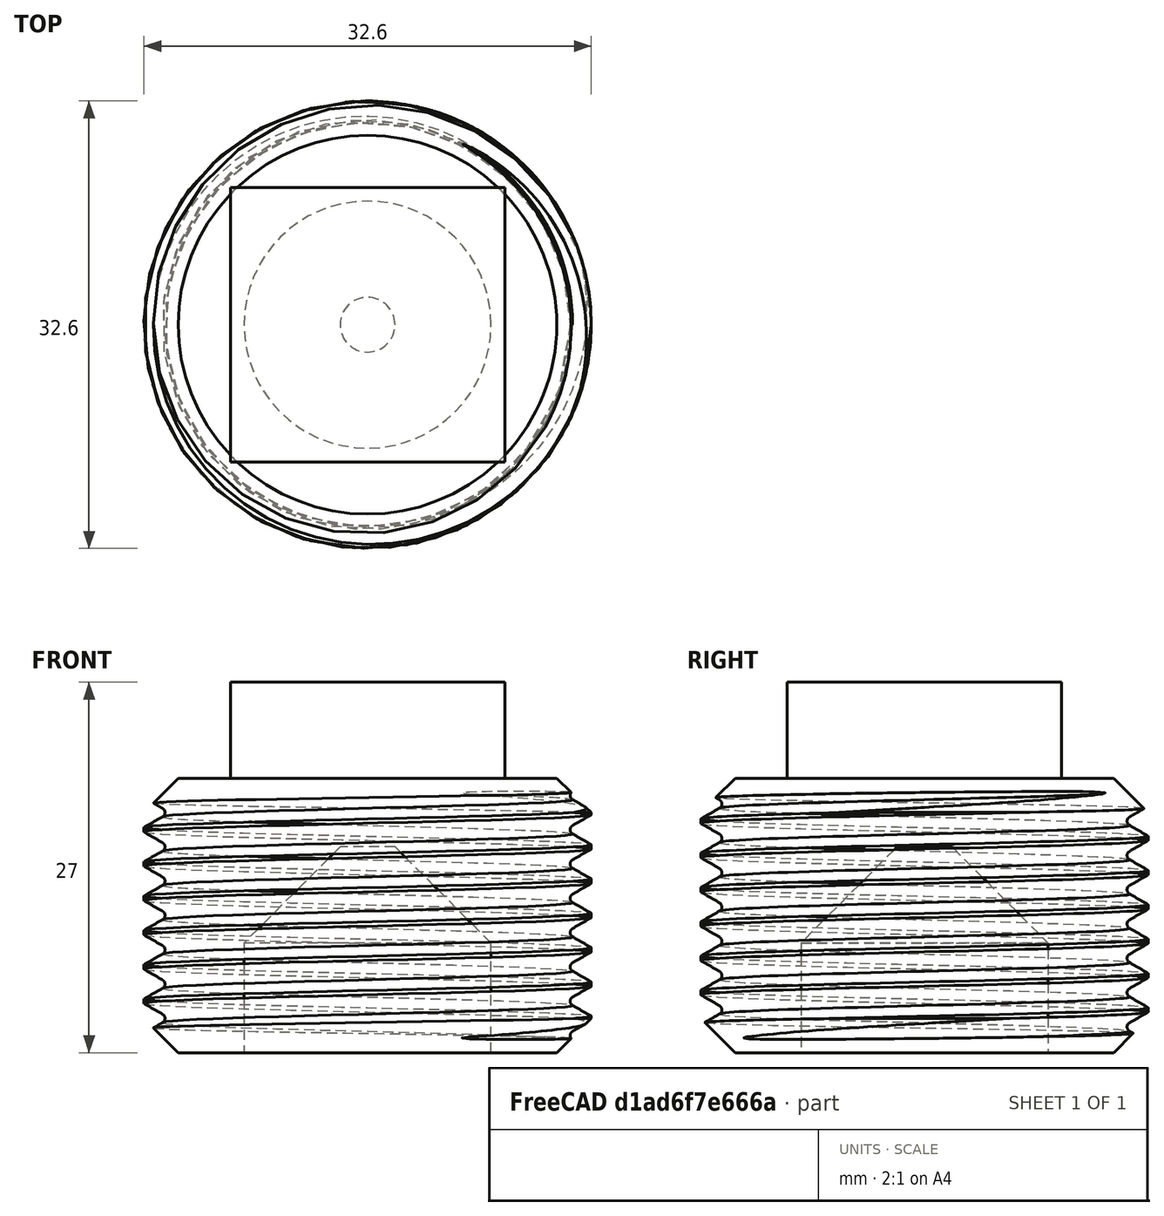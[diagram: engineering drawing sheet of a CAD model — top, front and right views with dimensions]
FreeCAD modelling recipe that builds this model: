
FCSTD DOCUMENT  (FreeCAD 1.1R40607 (Git))
Label: Резьба внешняя дюйм
License: All rights reserved
LicenseURL: https://en.wikipedia.org/wiki/All_rights_reserved
objects: Part::FeaturePython×1, App::Point×1, PartDesign::AdditiveBox×1, PartDesign::Body×1, Part::Cylinder×1, Part::Cut×1, Part::MultiFuse×1, Part::Chamfer×1
note: 9 computed .brp shape members not serialized (recipe doc carries the construction recipe); baked Part::Feature solids carry a one-line shape summary decoded from their .brp

FEATURE [Part::FeaturePython] ThreadedRod  label="32.6x20-Шпилька"  # WARN: FeaturePython — macro-defined, semantics opaque (R4)
  Diameter = 33
  DiameterCustom = 32.6
  Invert = false
  LeftHanded = false
  Length = 20
  MatchOuter = false
  OffsetAngle = 0
  PitchCustom = 2.5
  Thread = true
  Type = 5
FEATURE [App::Point] Origin001  label="Начало координат"
  Role = Origin
FEATURE [PartDesign::AdditiveBox] Box
  AttacherType = Attacher::AttachEngine3D
  Height = 7
  Length = 20
  Refine = true
  Suppressed = false
  Width = 20
FEATURE [PartDesign::Body] Body
  AllowCompound = false
  Group = -> [Box]
  Origin = -> Origin
  Placement = pos=(-10,-10,0) rot=(0,0,1;0rad)
  Tip = -> Box
FEATURE [Part::Cylinder] Cylinder  label="Цилиндр"
  Angle = 360
  AttacherType = Attacher::AttachEngine3D
  FirstAngle = 0
  Height = 15
  Placement = pos=(0,0,-20) rot=(0,0,1;0rad)
  Radius = 9
  SecondAngle = 0
FEATURE [Part::Cut] Cut
  Base = -> ThreadedRod
  Refine = true
  Tool = -> Cylinder
FEATURE [Part::MultiFuse] Fusion
  Refine = true
  Shapes = -> [Body,Cut]
FEATURE [Part::Chamfer] Chamfer
  Base = -> Fusion
  EdgeLinks = -> Fusion [Edge103]
  Edges = 1 edges r=7: [Edge103]
